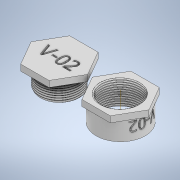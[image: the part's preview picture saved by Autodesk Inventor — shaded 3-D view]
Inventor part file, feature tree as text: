
AUTODESK INVENTOR PART (.ipt)
format: ipt  version: 2021.1 (Build 251245000, 245)  size: 922,624 bytes
history: native  units: in
note: dims shown in document units (in); Inventor stores cm internally (conversion verified against a paired STEP export)
features: sketch x9, extrude x6, helix x2, plane x1, other x1
ambient origin geometry x8: Origin, YZ Plane, XZ Plane, XY Plane, X Axis, Y Axis, Z Axis, Center Point
bodies: Body1 (feature_tree)
feature tree (19):
  extrude  "NutShaft"  Depth=1.0in
  helix  "CoilForNut"  [1 undecoded]
  extrude  "BoltHexHead"  Depth=0.0045in
  extrude  "BoltShaft"  Depth=0.0833in
  helix  "CoilForBolt"  [1 undecoded]
  extrude  "EmbossForBolt"  Depth=2.5in
  plane  "Work Plane4"
  other  "EmbossForNut"
  extrude  "NutHexHead"  Depth=0.25in
  extrude  "HoleForBolt"  Depth=0.75in TaperAngle=0.0deg
  sketch  "Sketch4"  dims[d4=2.0in d5=1.5528in d6=1.0in d7=0.0in]
  sketch  "Sketch6"  dims[d33=60.0deg d35=0.0045in]
  sketch  "Sketch7"  dims[d36=0.8224in d37=0.0833in d38=0.0833in]
  sketch  "Sketch8"  dims[d39=1.1667in d40=0.3937in d41=0.0in d42=90.0deg d43=90.0deg d44=0.0in d45=0.0in d46=2.5in]
  sketch  "Sketch9"  dims[d47=0.25in d48=0.0in d49=1.6118in]
  sketch  "Sketch11"  dims[d50=2.0in d51=0.75in d52=0.0in]
  sketch  "Sketch12"  dims[d53=60.0deg]
  sketch  "Sketch13"  dims[d54=0.0074in]
  sketch  "Sketch14"  dims[d56=0.8059in d57=0.7518in d58=0.0833in d59=1.0in d60=0.3937in d61=0.0in d62=90.0deg d63=90.0deg d64=0.0in d65=0.0in d66=0.0833in d68=0.1in d69=0.0in d70=1.0in d71=0.1in d72=0.0in d73=2.0in d74=0.25in d75=0.0in d76=0.75in d77=0.0in]
note: 2 required parameter values undecoded (feature->parameter linkage not recoverable at this tier; creation-order binding heuristic only, values carry confidence <= 0.55)
